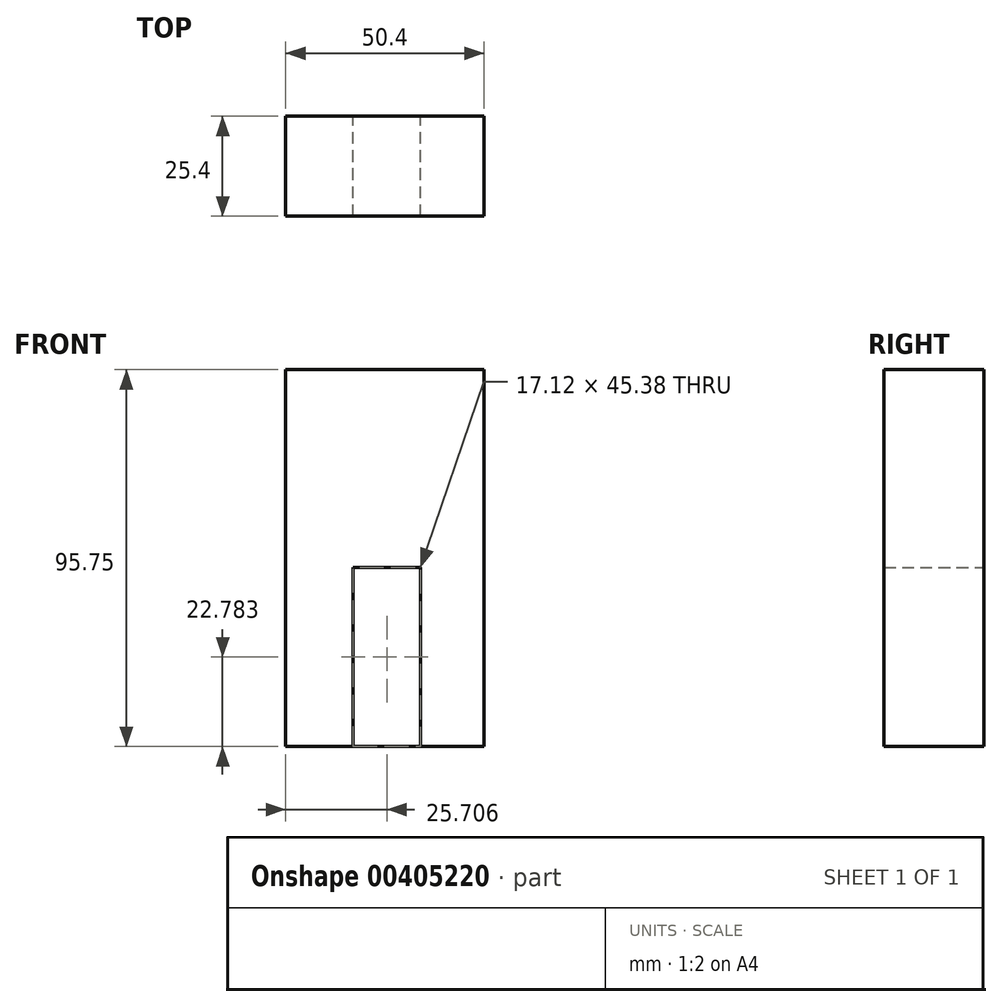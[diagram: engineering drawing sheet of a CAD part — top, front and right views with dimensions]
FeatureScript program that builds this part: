
annotation { "Feature Type Name" : "Feature", "Feature Type Description" : "" }
export const myFeature = defineFeature(function(context is Context, id is Id, definition is map)
    precondition{}
    {
        {
            var Q0;
            Q0=qCreatedBy(makeId("Top.planeOp"),FACE);
            var sketch = newSketch(context, id + "F0", { "sketchPlane" : qUnion([Q0])});
            skLineSegment(sketch, "E0.bottom", {"start": v(0, -34.2) * mm, "end": v(36.87, -34.2) * mm});
            skLineSegment(sketch, "E0.top", {"start": v(0, 12.16) * mm, "end": v(36.87, 12.16) * mm});
            skLineSegment(sketch, "E0.left", {"start": v(0, -34.2) * mm, "end": v(0, 12.16) * mm});
            skLineSegment(sketch, "E0.right", {"start": v(36.87, -34.2) * mm, "end": v(36.87, 12.16) * mm});
            skSolve(sketch);
        }
        {
            var Q0;
            Q0 = qSketchRegion(id + "F0", true);
            extrude(context, id + "F1", {"entities" : qUnion([Q0]), "depth" : 43.5 * mm});
        }
        {
            var Q0;
            Q0=makeQuery(id+"F1.opExtrude","SWEPT_BODY",BODY,{"disambiguationData":[OSD([sQuery(id+"F0.wireOp",EDGE,"E0.bottom"),sQuery(id+"F0.wireOp",EDGE,"E0.top"),sQuery(id+"F0.wireOp",EDGE,"E0.left"),sQuery(id+"F0.wireOp",EDGE,"E0.right")])]});
            deleteBodies(context, id + "F2", {"entities" : qUnion([Q0])});
        }
        {
            var Q0;
            Q0=qCreatedBy(makeId("Front.planeOp"),FACE);
            var sketch = newSketch(context, id + "F3", { "sketchPlane" : qUnion([Q0])});
            skLineSegment(sketch, "E1", {"start": v(-25.47, -12.46) * mm, "end": v(-25.47, 46.14) * mm});
            skLineSegment(sketch, "E2", {"start": v(-25.47, 46.14) * mm, "end": v(-25.47, 46.14) * mm});
            skLineSegment(sketch, "E3", {"start": v(-25.47, 46.14) * mm, "end": v(25.96, 46.14) * mm});
            skLineSegment(sketch, "E4.bottom", {"start": v(-25.84, 48.77) * mm, "end": v(-25.47, 48.77) * mm});
            skLineSegment(sketch, "E4.top", {"start": v(-25.84, 46.14) * mm, "end": v(-25.47, 46.14) * mm});
            skLineSegment(sketch, "E4.left", {"start": v(-25.84, 48.77) * mm, "end": v(-25.84, 46.14) * mm});
            skLineSegment(sketch, "E4.right", {"start": v(-25.47, 48.77) * mm, "end": v(-25.47, 46.14) * mm});
            skLineSegment(sketch, "E5.bottom", {"start": v(28.9, -10.63) * mm, "end": v(-21.5, -10.63) * mm});
            skLineSegment(sketch, "E5.top", {"start": v(28.9, 85.12) * mm, "end": v(-21.5, 85.12) * mm});
            skLineSegment(sketch, "E5.left", {"start": v(28.9, -10.63) * mm, "end": v(28.9, 85.12) * mm});
            skLineSegment(sketch, "E5.right", {"start": v(-21.5, -10.63) * mm, "end": v(-21.5, 85.12) * mm});
            skPoint(sketch, "E6.oppositeSnap0", {"position": v(-21.5, 37.25) * mm});
            skLineSegment(sketch, "E6.bottom", {"start": v(-21.5, 37.25) * mm, "end": v(-25.47, 37.25) * mm, "construction": true});
            skLineSegment(sketch, "E6.top", {"start": v(-21.5, 37.25) * mm, "end": v(-25.47, 37.25) * mm, "construction": true});
            skLineSegment(sketch, "E6.left", {"start": v(-21.5, 37.25) * mm, "end": v(-21.5, 37.25) * mm});
            skLineSegment(sketch, "E6.right", {"start": v(-25.47, 37.25) * mm, "end": v(-25.47, 37.25) * mm});
            skSolve(sketch);
        }
        {
            var Q0;
            {var subQ0=sQuery(id+"F3.wireOp",EDGE,"E5.bottom");Q0=makeQuery(id+"F3.imprint","IMPRINT",FACE,{"disambiguationData":[TD([[makeQuery(id+"F3.imprint","IMPRINT",EDGE,{"derivedFrom":subQ0}),-1.0]])]});}
            extrude(context, id + "F4", {"entities" : qUnion([Q0]), "depth" : 25.4 * mm});
        }
        {
            var Q0;
            Q0=qCreatedBy(makeId("Front.planeOp"),FACE);
            var sketch = newSketch(context, id + "F5", { "sketchPlane" : qUnion([Q0])});
            skLineSegment(sketch, "E7.bottom", {"start": v(-4.35, -10.54) * mm, "end": v(12.77, -10.54) * mm});
            skLineSegment(sketch, "E7.top", {"start": v(-4.35, 34.85) * mm, "end": v(12.77, 34.85) * mm});
            skLineSegment(sketch, "E7.left", {"start": v(-4.35, -10.54) * mm, "end": v(-4.35, 34.85) * mm});
            skLineSegment(sketch, "E7.right", {"start": v(12.77, -10.54) * mm, "end": v(12.77, 34.85) * mm});
            skLineSegment(sketch, "E8.bottom", {"start": v(-3.05, 0) * mm, "end": v(-4.35, 0) * mm});
            skLineSegment(sketch, "E8.top", {"start": v(-3.05, 0) * mm, "end": v(-4.35, 0) * mm});
            skLineSegment(sketch, "E8.left", {"start": v(-3.05, 0) * mm, "end": v(-3.05, 0) * mm});
            skLineSegment(sketch, "E8.right", {"start": v(-4.35, 0) * mm, "end": v(-4.35, 0) * mm});
            skSolve(sketch);
        }
        {
            var Q0;
            Q0=makeQuery(id+"F4.opExtrude","CAP_FACE",FACE,{"disambiguationData":[OSD([sQuery(id+"F3.wireOp",EDGE,"E5.bottom"),sQuery(id+"F3.wireOp",EDGE,"E5.top"),sQuery(id+"F3.wireOp",EDGE,"E5.left"),sQuery(id+"F3.wireOp",EDGE,"E5.right")])],"isStart":false});
            var Q1;
            {var subQ3=sQuery(id+"F5.wireOp",EDGE,"E7.bottom");Q1=makeQuery(id+"F5.imprint","IMPRINT",FACE,{"disambiguationData":[TD([[makeQuery(id+"F5.imprint","IMPRINT",EDGE,{"derivedFrom":subQ3}),1.0]])]});}
            extrude(context, id + "F6", {"entities" : qUnion([Q0, Q1]), "operationType" : NewBodyOperationType.REMOVE, "depth" : 80.47 * mm});
        }
    });
